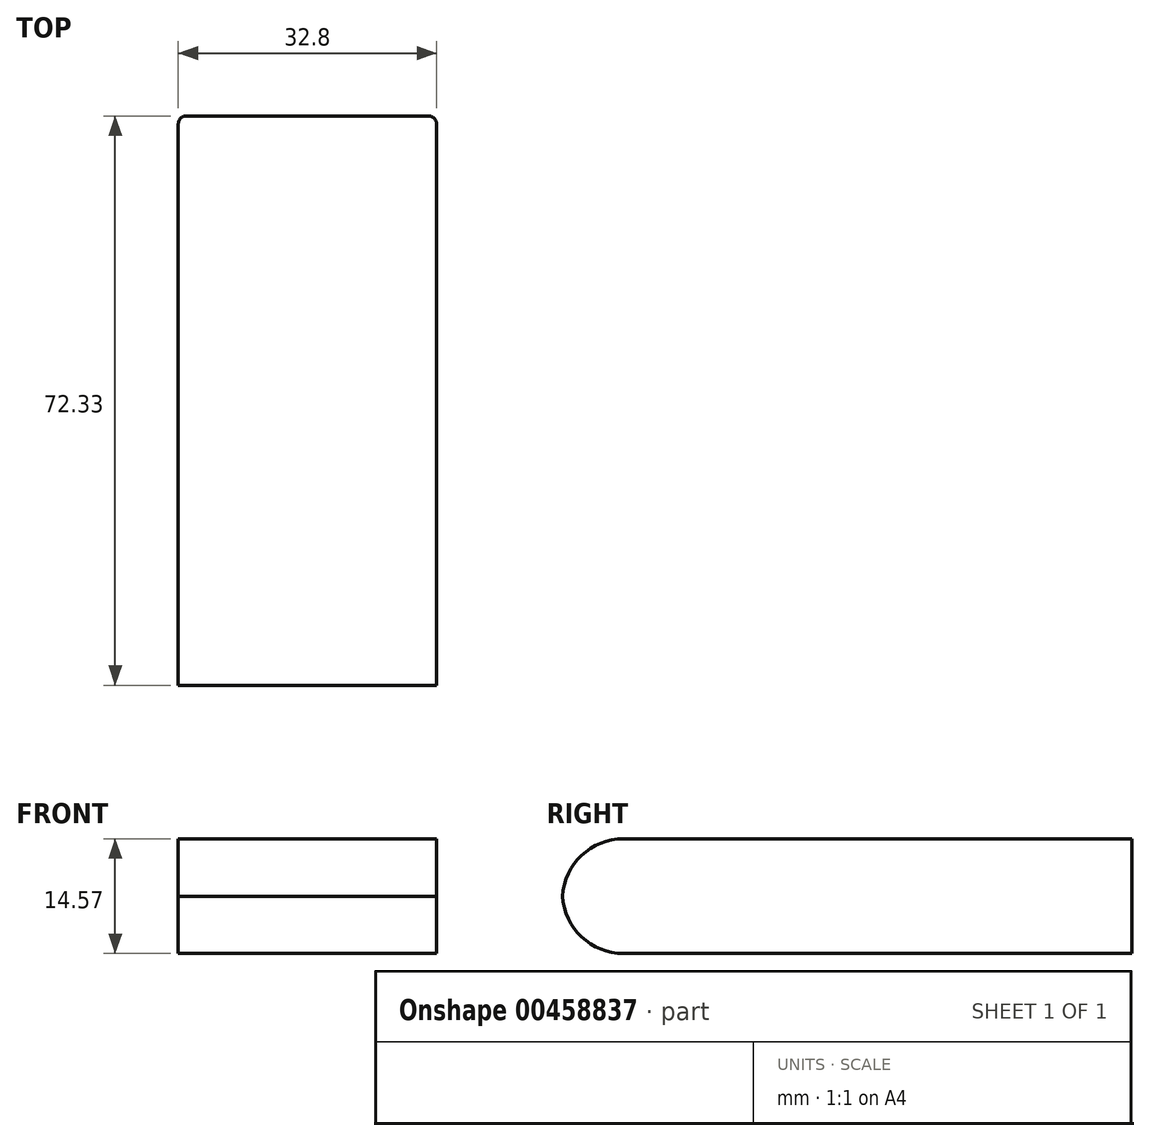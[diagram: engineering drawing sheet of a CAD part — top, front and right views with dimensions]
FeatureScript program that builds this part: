
annotation { "Feature Type Name" : "Feature", "Feature Type Description" : "" }
export const myFeature = defineFeature(function(context is Context, id is Id, definition is map)
    precondition{}
    {
        {
            var Q0;
            Q0=qCreatedBy(makeId("Front.planeOp"),FACE);
            var sketch = newSketch(context, id + "F0", { "sketchPlane" : qUnion([Q0])});
            skLineSegment(sketch, "E0.bottom", {"start": v(0, 0) * mm, "end": v(32.8, 0) * mm});
            skLineSegment(sketch, "E0.top", {"start": v(0, 14.57) * mm, "end": v(32.8, 14.57) * mm});
            skLineSegment(sketch, "E0.left", {"start": v(0, 0) * mm, "end": v(0, 14.57) * mm});
            skLineSegment(sketch, "E0.right", {"start": v(32.8, 0) * mm, "end": v(32.8, 14.57) * mm});
            skSolve(sketch);
        }
        {
            var Q0;
            Q0 = qSketchRegion(id + "F0", true);
            extrude(context, id + "F1", {"entities" : qUnion([Q0]), "depth" : 72.34 * mm, "offsetDistance" : 25 * mm});
        }
        {
            var Q0;
            Q0=makeQuery(id+"F1.opExtrude","CAP_EDGE",EDGE,{"disambiguationData":[OSD([sQuery(id+"F0.wireOp",EDGE,"E0.top")])],"isStart":false});
            var Q1;
            Q1=makeQuery(id+"F1.opExtrude","CAP_EDGE",EDGE,{"disambiguationData":[OSD([sQuery(id+"F0.wireOp",EDGE,"E0.bottom")])],"isStart":false});
            fillet(context, id + "F2", {"entities" : qUnion([Q0, Q1]), "radius" : 7.75 * mm, "tangentPropagation" : true, "allowEdgeOverflow" : false});
        }
        {
            var Q0;
            Q0=makeQuery(id+"F1.opExtrude","CAP_EDGE",EDGE,{"disambiguationData":[OSD([sQuery(id+"F0.wireOp",EDGE,"E0.left")])],"isStart":true});
            var Q1;
            Q1=makeQuery(id+"F1.opExtrude","CAP_EDGE",EDGE,{"disambiguationData":[OSD([sQuery(id+"F0.wireOp",EDGE,"E0.right")])],"isStart":true});
            fillet(context, id + "F3", {"entities" : qUnion([Q0, Q1]), "radius" : 1 * mm, "tangentPropagation" : true, "allowEdgeOverflow" : false});
        }
    });
